# Revit family: Hager-UNIVERS-Surface_mounted-IP44-With_Cover-With_DIN-Hosted-CH-fr
name_source: partatom
category: Electrical Equipment
units: mm (PartAtom-declared; Revit-internal decimal feet)

## family parameters
Cut with Voids When Loaded = No
Host = Face
Maintain Annotation Orientation = Yes
Panel Configuration = Two Columns, Circuits Across
Part Type = Panelboard
Room Calculation Point = No
Round Connector Dimension = Use Diameter
Shared = No

## types (37) — shared parameters
BC_MODEL_ID = 1539177
BC_OBJECT_ID = 512280
BC_OBJECT_VERSION = #59
Code hager = ADD-EC000214_EU
EF000007 - couleur = blanc
EF000024 - résiste aux UV = No
EF000049 - profondeur = 165 mm  [stored 0.541339 ft]
EF000116 - numéro RAL = 9010
EF001062 - version CEM = No
EF001088 - possibilité de montage adossé = Yes
EF001134 - rail DIN = Yes
EF004462 - type de fermeture = autre
EF005474 - indice de protection (IP) = IP44
EF006244 - couvercle/porte transparente = No
EF006306 - avec serrure = No
EF015941 - porte de transmission du signal = No
ETIM class code = EC000214
ETIM class name = Small distribution board
HG000002-avec porte = Yes
HG000003-Gamme = UNIVERS
HG000005-Epaisseur = 2 mm  [stored 0.00656168 ft]
HG000006-Encastré = No
HG000011-Rangées du bas vides = No
HG000012-Angle de pivotement de la porte = 90.00°
HG000013-Porte à gauche = No
HG000014-Porte à droite = Yes
HG000015-Visibilité de l'emprise de la porte = Yes
HG000016-Visibilité de la porte 3D = Yes
HG000017-Distance entre pôles = 18 mm  [stored 0.0590551 ft]
HG000060-RAL-number = 9010
HG000099-ID modèle Onfly = 507532
Manufacturer = Hager
Name = UNIVERS-Surface_mounted-IP44-With_Cover-With_DIN-CH
Name BIM&CO = Electricity
Name hager = ADD_Enclosures_EC000214
Uniformat = Low Tension Service & Dist.
Uniformat code = D501001
zero-valued in all types: Default Elevation, EF001131 - profondeur interne

## per-type parameters (varying)
| type | BC_VARIANT_ID | EF000003 - mode de montage | EF000008 - largeur | EF000040 - hauteur | EF000118 - avec plaque de montage | EF000218 - profondeur de montage | EF000266 - nombre de rangées | EF000332 - hauteur d'installation | EF000846 - largeur d'encastrement | EF002950 - nombre d'unités modulaires | EF009212 - type de couvercle | EF015776 - borne de mise à la terre | EF015777 - borne à conducteur neutre | HG000001-nombre de colonnes | HG000004-Référence fabricant | HG000007-Nombre de colonnes vides | HG000008-Nombre de rangées vides | HG000009-Porte à double battant | HG000010-Portes asymétriques | HGEF000266-Nombre de rangées | HGEF0002950-largeur en nombre de modules |
| UNIVERS-Surface_mounted_W300_H500_D165_12_Modular_Spacing-FWB31S | 1169607 | apparent | 300 mm | 500 mm  [stored 1.64042 ft] | No | 161 mm  [stored 0.528215 ft] | 3 | 500 mm  [stored 1.64042 ft] | 300 mm | 12 | avec découpe | Yes | Yes | 1 | FWB31S | 0 | 0 | No | No | 3 | 12 |
| UNIVERS-Surface_mounted_W550_H500_D165_24_Modular_Spacing-FWB32S | 1169623 | apparent | 550 mm | 500 mm  [stored 1.64042 ft] | No | 161 mm  [stored 0.528215 ft] | 3 | 500 mm  [stored 1.64042 ft] | 550 mm | 24 | avec découpe | Yes | Yes | 2 | FWB32S | 0 | 0 | No | No | 3 | 24 |
| UNIVERS-Surface_mounted_W800_H500_D165_36_Modular_Spacing-FWB33S | 1169630 | apparent | 800 mm  [stored 2.62467 ft] | 500 mm  [stored 1.64042 ft] | No | 161 mm  [stored 0.528215 ft] | 3 | 500 mm  [stored 1.64042 ft] | 800 mm  [stored 2.62467 ft] | 36 | avec découpe | Yes | Yes | 3 | FWB33S | 0 | 0 | Yes | Yes | 3 | 36 |
| UNIVERS-Surface_mounted_W1050_H500_D165_48_Modular_Spacing-FWB34S | 1169637 | apparent | 1050 mm | 500 mm  [stored 1.64042 ft] | No | 161 mm  [stored 0.528215 ft] | 3 | 500 mm  [stored 1.64042 ft] | 1050 mm | 48 | avec découpe | Yes | Yes | 4 | FWB34S | 0 | 0 | Yes | No | 3 | 48 |
| UNIVERS-Surface_mounted_W300_H650_D165_12_Modular_Spacing-FWB41S | 1169643 | apparent | 300 mm | 650 mm  [stored 2.13255 ft] | No | 161 mm  [stored 0.528215 ft] | 4 | 650 mm  [stored 2.13255 ft] | 300 mm | 12 | avec découpe | Yes | Yes | 1 | FWB41S | 0 | 0 | No | No | 4 | 12 |
| UNIVERS-Surface_mounted_W550_H650_D165_24_Modular_Spacing-FWB42K5 | 1169650 | apparent | 550 mm | 650 mm  [stored 2.13255 ft] | Yes | 161 mm  [stored 0.528215 ft] | 4 | 650 mm  [stored 2.13255 ft] | 550 mm | 24 | avec découpe | Yes | No | 2 | FWB42K5 | 1 | 0 | No | No | 4 | 24 |
| UNIVERS-Surface_mounted_W550_H650_D165_24_Modular_Spacing-FWB42P2 | 1169656 | apparent/encastré | 550 mm | 650 mm  [stored 2.13255 ft] | No | 161 mm  [stored 0.528215 ft] | 4 | 650 mm  [stored 2.13255 ft] | 550 mm | 24 | avec découpe | Yes | No | 1 | FWB42P2 | 1 | 0 | No | No | 4 | 24 |
| UNIVERS-Surface_mounted_W550_H650_D165_24_Modular_Spacing-FWB42S | 1169662 | apparent/encastré | 550 mm | 650 mm  [stored 2.13255 ft] | No | 161 mm  [stored 0.528215 ft] | 4 | 650 mm  [stored 2.13255 ft] | 550 mm | 24 | avec découpe | Yes | Yes | 2 | FWB42S | 0 | 0 | No | No | 4 | 24 |
| UNIVERS-Surface_mounted_W800_H650_D165_36_Modular_Spacing-FWB43S | 1169668 | apparent | 800 mm  [stored 2.62467 ft] | 650 mm  [stored 2.13255 ft] | No | 161 mm  [stored 0.528215 ft] | 4 | 650 mm  [stored 2.13255 ft] | 800 mm  [stored 2.62467 ft] | 36 | avec découpe | Yes | Yes | 3 | FWB43S | 0 | 0 | Yes | Yes | 4 | 36 |
| UNIVERS-Surface_mounted_W1050_H650_D165_48_Modular_Spacing-FWB44S | 1169673 | apparent | 1050 mm | 650 mm  [stored 2.13255 ft] | No | 161 mm  [stored 0.528215 ft] | 4 | 650 mm  [stored 2.13255 ft] | 1050 mm | 48 | avec découpe | Yes | Yes | 4 | FWB44S | 0 | 0 | Yes | No | 4 | 48 |
| UNIVERS-Surface_mounted_W300_H800_D165_12_Modular_Spacing-FWB51S | 1169678 | apparent | 300 mm | 800 mm  [stored 2.62467 ft] | No | 161 mm  [stored 0.528215 ft] | 5 | 800 mm  [stored 2.62467 ft] | 300 mm | 12 | avec découpe | Yes | Yes | 1 | FWB51S | 0 | 0 | No | No | 5 | 12 |
| UNIVERS-Surface_mounted_W550_H800_D165_24_Modular_Spacing-FWB52K5 | 1169683 | apparent | 550 mm | 800 mm  [stored 2.62467 ft] | Yes | 161 mm  [stored 0.528215 ft] | 5 | 800 mm  [stored 2.62467 ft] | 550 mm | 24 | avec découpe | Yes | No | 2 | FWB52K5 | 1 | 0 | No | No | 5 | 24 |
| UNIVERS-Surface_mounted_W550_H800_D165_24_Modular_Spacing-FWB52N3 | 1169688 | apparent | 550 mm | 800 mm  [stored 2.62467 ft] | No | 160 mm  [stored 0.524934 ft] | 5 | 800 mm  [stored 2.62467 ft] | 550 mm | 24 | avec découpe | No | No | 2 | FWB52N3 | 0 | 2 | No | No | 5 | 24 |
| UNIVERS-Surface_mounted_W550_H800_D165_24_Modular_Spacing-FWB52P2 | 1169693 | apparent/encastré | 550 mm | 800 mm  [stored 2.62467 ft] | No | 161 mm  [stored 0.528215 ft] | 5 | 800 mm  [stored 2.62467 ft] | 550 mm | 24 | avec découpe | Yes | No | 1 | FWB52P2 | 1 | 0 | No | No | 5 | 24 |
| UNIVERS-Surface_mounted_W550_H800_D165_24_Modular_Spacing-FWB52S | 1169698 | apparent | 550 mm | 800 mm  [stored 2.62467 ft] | No | 161 mm  [stored 0.528215 ft] | 5 | 800 mm  [stored 2.62467 ft] | 550 mm | 24 | avec découpe | Yes | Yes | 2 | FWB52S | 0 | 0 | No | No | 5 | 24 |
| UNIVERS-Surface_mounted_W800_H800_D165_36_Modular_Spacing-FWB53K5 | 1169704 | apparent | 800 mm  [stored 2.62467 ft] | 800 mm  [stored 2.62467 ft] | Yes | 161 mm  [stored 0.528215 ft] | 5 | 800 mm  [stored 2.62467 ft] | 800 mm  [stored 2.62467 ft] | 36 | avec découpe | Yes | No | 2 | FWB53K5 | 1 | 0 | Yes | Yes | 5 | 36 |
| UNIVERS-Surface_mounted_W800_H800_D165_36_Modular_Spacing-FWB53N3 | 1169705 | apparent | 800 mm  [stored 2.62467 ft] | 800 mm  [stored 2.62467 ft] | No | 161 mm  [stored 0.528215 ft] | 5 | 800 mm  [stored 2.62467 ft] | 800 mm  [stored 2.62467 ft] | 36 | avec découpe | No | No | 3 | FWB53N3 | 0 | 2 | Yes | Yes | 5 | 36 |
| UNIVERS-Surface_mounted_W800_H800_D165_36_Modular_Spacing-FWB53S | 1169706 | apparent | 800 mm  [stored 2.62467 ft] | 800 mm  [stored 2.62467 ft] | No | 161 mm  [stored 0.528215 ft] | 5 | 800 mm  [stored 2.62467 ft] | 800 mm  [stored 2.62467 ft] | 36 | avec découpe | Yes | Yes | 3 | FWB53S | 0 | 0 | Yes | Yes | 5 | 36 |
| UNIVERS-Surface_mounted_W1050_H800_D165_48_Modular_Spacing-FWB54S | 1169707 | apparent | 1050 mm | 800 mm  [stored 2.62467 ft] | No | 161 mm  [stored 0.528215 ft] | 5 | 800 mm  [stored 2.62467 ft] | 1050 mm | 48 | avec découpe | Yes | Yes | 4 | FWB54S | 0 | 0 | Yes | No | 5 | 48 |
| UNIVERS-Surface_mounted_W300_H950_D165_12_Modular_Spacing-FWB61S | 1169709 | apparent | 300 mm | 950 mm  [stored 3.1168 ft] | No | 161 mm  [stored 0.528215 ft] | 6 | 950 mm  [stored 3.1168 ft] | 300 mm | 12 | avec découpe | Yes | Yes | 1 | FWB61S | 0 | 0 | No | No | 6 | 12 |
| UNIVERS-Surface_mounted_W550_H950_D165_24_Modular_Spacing-FWB62K5 | 1169714 | apparent | 550 mm | 950 mm  [stored 3.1168 ft] | Yes | 161 mm  [stored 0.528215 ft] | 6 | 950 mm  [stored 3.1168 ft] | 550 mm | 24 | avec découpe | Yes | No | 1 | FWB62K5 | 1 | 0 | No | No | 6 | 24 |
| UNIVERS-Surface_mounted_W550_H950_D165_24_Modular_Spacing-FWB62N3 | 1169719 | apparent | 550 mm | 950 mm  [stored 3.1168 ft] | No | 161 mm  [stored 0.528215 ft] | 6 | 950 mm  [stored 3.1168 ft] | 550 mm | 24 | avec découpe | No | No | 2 | FWB62N3 | 0 | 2 | No | No | 6 | 24 |
| UNIVERS-Surface_mounted_W550_H950_D165_24_Modular_Spacing-FWB62S | 1169723 | apparent | 550 mm | 950 mm  [stored 3.1168 ft] | No | 161 mm  [stored 0.528215 ft] | 6 | 950 mm  [stored 3.1168 ft] | 550 mm | 24 | avec découpe | Yes | Yes | 2 | FWB62S | 0 | 0 | No | No | 6 | 24 |
| UNIVERS-Surface_mounted_W800_H950_D165_36_Modular_Spacing-FWB63K5 | 1169728 | apparent | 800 mm  [stored 2.62467 ft] | 950 mm  [stored 3.1168 ft] | Yes | 161 mm  [stored 0.528215 ft] | 6 | 950 mm  [stored 3.1168 ft] | 800 mm  [stored 2.62467 ft] | 36 | avec découpe | Yes | No | 2 | FWB63K5 | 1 | 0 | Yes | Yes | 6 | 36 |
| UNIVERS-Surface_mounted_W800_H950_D165_36_Modular_Spacing-FWB63N3 | 1169732 | apparent | 800 mm  [stored 2.62467 ft] | 950 mm  [stored 3.1168 ft] | No | 161 mm  [stored 0.528215 ft] | 6 | 950 mm  [stored 3.1168 ft] | 800 mm  [stored 2.62467 ft] | 36 | avec découpe | No | No | 3 | FWB63N3 | 0 | 2 | Yes | Yes | 6 | 36 |
| UNIVERS-Surface_mounted_W800_H950_D165_36_Modular_Spacing-FWB63S | 1169737 | apparent | 800 mm  [stored 2.62467 ft] | 950 mm  [stored 3.1168 ft] | No | 161 mm  [stored 0.528215 ft] | 6 | 950 mm  [stored 3.1168 ft] | 800 mm  [stored 2.62467 ft] | 36 | avec découpe | Yes | Yes | 3 | FWB63S | 0 | 0 | Yes | Yes | 6 | 36 |
| UNIVERS-Surface_mounted_W1050_H950_D165_48_Modular_Spacing-FWB64N3 | 1169742 | apparent | 1050 mm | 950 mm  [stored 3.1168 ft] | No | 161 mm  [stored 0.528215 ft] | 6 | 950 mm  [stored 3.1168 ft] | 1050 mm | 48 | avec découpe | No | No | 4 | FWB64N3 | 0 | 2 | Yes | No | 6 | 48 |
| UNIVERS-Surface_mounted_W1050_H950_D165_48_Modular_Spacing-FWB64S | 1169744 | apparent | 1050 mm | 950 mm  [stored 3.1168 ft] | No | 161 mm  [stored 0.528215 ft] | 6 | 950 mm  [stored 3.1168 ft] | 1050 mm | 48 | avec découpe | Yes | Yes | 4 | FWB64S | 0 | 0 | Yes | No | 6 | 48 |
| UNIVERS-Surface_mounted_W300_H1100_D165_12_Modular_Spacing-FWB71S | 1169745 | apparent | 300 mm | 1100 mm | No | 161 mm  [stored 0.528215 ft] | 7 | 1100 mm | 300 mm | 12 | avec découpe | Yes | Yes | 1 | FWB71S | 0 | 0 | No | No | 7 | 12 |
| UNIVERS-Surface_mounted_W550_H1100_D165_24_Modular_Spacing-FWB72K5 | 1169746 | apparent | 550 mm | 1100 mm | Yes | 161 mm  [stored 0.528215 ft] | 7 | 1100 mm | 550 mm | 24 | avec découpe | Yes | No | 1 | FWB72K5 | 1 | 0 | No | No | 7 | 24 |
| UNIVERS-Surface_mounted_W550_H1100_D165_24_Modular_Spacing-FWB72N3 | 1169747 | apparent | 550 mm | 1100 mm | No | 161 mm  [stored 0.528215 ft] | 7 | 1100 mm | 550 mm | 24 | avec découpe | No | No | 2 | FWB72N3 | 0 | 2 | No | No | 7 | 24 |
| UNIVERS-Surface_mounted_W550_H1100_D165_24_Modular_Spacing-FWB72S | 1169748 | apparent/encastré | 550 mm | 1100 mm | No | 161 mm  [stored 0.528215 ft] | 7 | 1100 mm | 550 mm | 24 | avec découpe | Yes | Yes | 2 | FWB72S | 0 | 0 | No | No | 7 | 24 |
| UNIVERS-Surface_mounted_W800_H1100_D165_36_Modular_Spacing-FWB73N3 | 1169749 | apparent | 800 mm  [stored 2.62467 ft] | 1100 mm | No | 161 mm  [stored 0.528215 ft] | 7 | 1100 mm | 800 mm  [stored 2.62467 ft] | 36 | avec découpe | No | No | 3 | FWB73N3 | 0 | 2 | Yes | Yes | 7 | 36 |
| UNIVERS-Surface_mounted_W800_H1100_D165_36_Modular_Spacing-FWB73S | 1169750 | apparent/encastré | 800 mm  [stored 2.62467 ft] | 1100 mm | No | 161 mm  [stored 0.528215 ft] | 7 | 1100 mm | 800 mm  [stored 2.62467 ft] | 36 | avec découpe | Yes | Yes | 3 | FWB73S | 0 | 0 | Yes | Yes | 7 | 36 |
| UNIVERS-Surface_mounted_W1050_H1100_D165_48_Modular_Spacing-FWB74N3 | 1169751 | apparent | 1050 mm | 1100 mm | No | 161 mm  [stored 0.528215 ft] | 7 | 1100 mm | 1050 mm | 48 | avec découpe | No | No | 4 | FWB74N3 | 0 | 2 | Yes | No | 7 | 48 |
| UNIVERS-Surface_mounted_W1050_H1100_D165_48_Modular_Spacing-FWB74S | 1169752 | apparent/encastré | 1050 mm | 1100 mm | No | 161 mm  [stored 0.528215 ft] | 7 | 1100 mm | 1050 mm | 48 | avec découpe | Yes | Yes | 4 | FWB74S | 0 | 0 | Yes | No | 7 | 48 |
| UNIVERS-Surface_mounted_W300_H1250_D165_12_Modular_Spacing-FWB81S | 1169753 | apparent | 300 mm | 1250 mm  [stored 4.10105 ft] | No | 161 mm  [stored 0.528215 ft] | 8 | 1250 mm  [stored 4.10105 ft] | 300 mm | 12 | fermé | Yes | Yes | 1 | FWB81S | 0 | 0 | No | No | 8 | 12 |

note: column(s) folded — value = type name in every type: Reference

note: [stored X ft] marks values corroborated as IEEE doubles in the binary element streams (Revit-internal decimal feet)

## geometry (parser evidence)
native form markers: Sweep x15
no freeform markers — native parametric forms only
